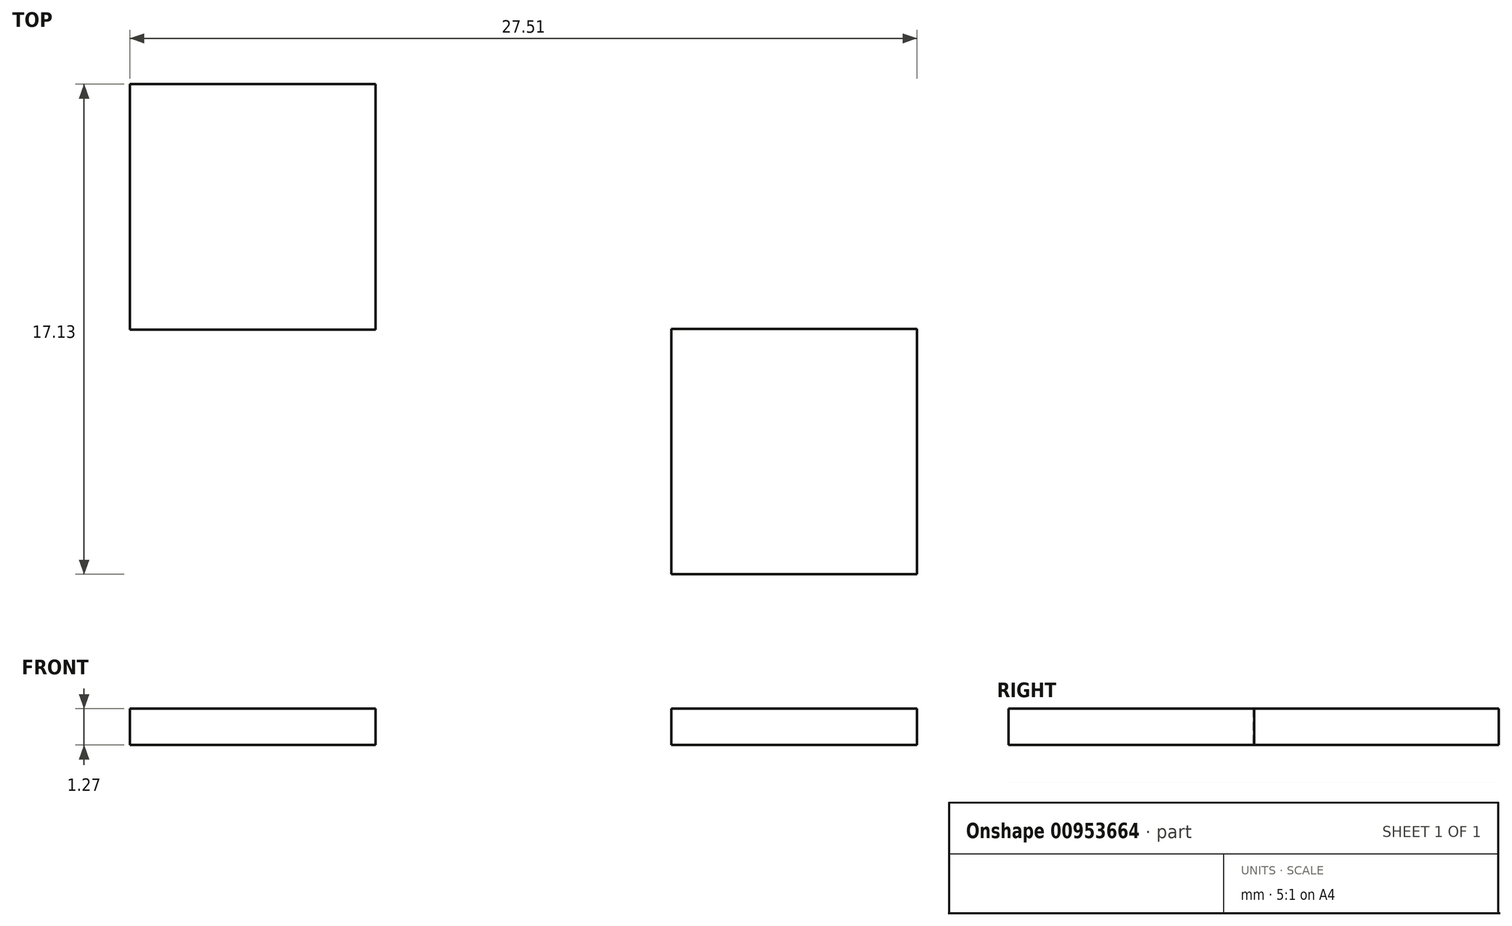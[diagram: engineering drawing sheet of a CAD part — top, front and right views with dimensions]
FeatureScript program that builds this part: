
annotation { "Feature Type Name" : "Feature", "Feature Type Description" : "" }
export const myFeature = defineFeature(function(context is Context, id is Id, definition is map)
    precondition{}
    {
        {
            var Q0;
            Q0=qCreatedBy(makeId("Top.planeOp"),FACE);
            var sketch = newSketch(context, id + "F0", { "sketchPlane" : qUnion([Q0])});
            skLineSegment(sketch, "E0.bottom", {"start": v(-23.22, 12.84) * mm, "end": v(-14.63, 12.84) * mm});
            skLineSegment(sketch, "E0.top", {"start": v(-23.22, 4.26) * mm, "end": v(-14.63, 4.26) * mm});
            skLineSegment(sketch, "E0.left", {"start": v(-23.22, 12.84) * mm, "end": v(-23.22, 4.26) * mm});
            skLineSegment(sketch, "E0.right", {"start": v(-14.63, 12.84) * mm, "end": v(-14.63, 4.26) * mm});
            skLineSegment(sketch, "E1.bottom", {"start": v(-4.3, 4.3) * mm, "end": v(4.3, 4.3) * mm});
            skLineSegment(sketch, "E1.top", {"start": v(-4.3, -4.3) * mm, "end": v(4.3, -4.3) * mm});
            skLineSegment(sketch, "E1.left", {"start": v(-4.3, 4.3) * mm, "end": v(-4.3, -4.3) * mm});
            skLineSegment(sketch, "E1.right", {"start": v(4.3, 4.3) * mm, "end": v(4.3, -4.3) * mm});
            skSolve(sketch);
        }
        {
            var Q0;
            Q0 = qSketchRegion(id + "F0", true);
            extrude(context, id + "F1", {"entities" : qUnion([Q0]), "depth" : 1.27 * mm, "offsetDistance" : 25.4 * mm});
        }
    });
